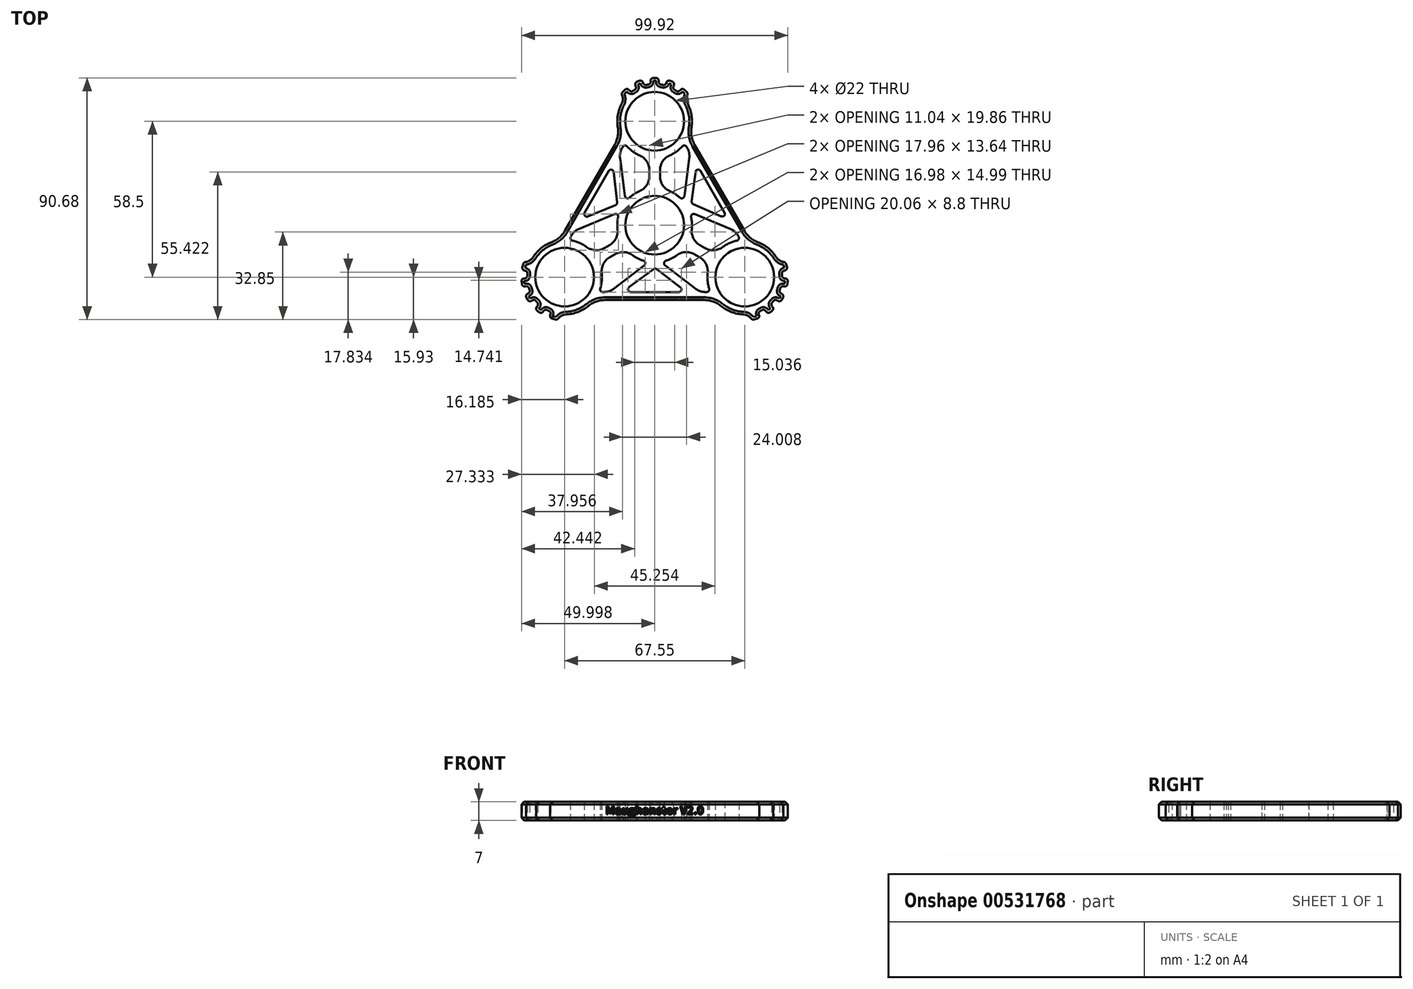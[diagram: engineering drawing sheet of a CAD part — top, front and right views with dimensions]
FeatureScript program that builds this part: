
annotation { "Feature Type Name" : "Feature", "Feature Type Description" : "" }
export const myFeature = defineFeature(function(context is Context, id is Id, definition is map)
    precondition{}
    {
        {
            var Q0;
            Q0=qCreatedBy(makeId("Top.planeOp"),FACE);
            var sketch = newSketch(context, id + "F0", { "sketchPlane" : qUnion([Q0])});
            skCircle(sketch, "E0", {"center": v(0, 0) * mm, "radius": 11 * mm});
            skArc(sketch, "E1.0", {"start": v(-2, 13.86) * mm, "mid": v(-6.9, 12.18) * mm, "end": v(-10.85, 8.84) * mm});
            skCircle(sketch, "E2", {"center": v(0, 39) * mm, "radius": 11 * mm});
            skArc(sketch, "E3.0", {"start": v(-10.9, 47.78) * mm, "mid": v(-13.85, 41.03) * mm, "end": v(-12.97, 33.72) * mm});
            skLineSegment(sketch, "E4", {"start": v(0, 11) * mm, "end": v(0, 28) * mm, "construction": true});
            skLineSegment(sketch, "E5.0", {"start": v(2, 13.86) * mm, "end": v(2, 25.14) * mm});
            skLineSegment(sketch, "E6.0", {"start": v(-2, 13.86) * mm, "end": v(-2, 25.14) * mm});
            skLineSegment(sketch, "E7", {"start": v(0, 53) * mm, "end": v(0, 55) * mm, "construction": true});
            skLineSegment(sketch, "E8.0", {"start": v(1.5, 52.92) * mm, "end": v(1.5, 55.25) * mm});
            skLineSegment(sketch, "E9.0", {"start": v(-1.5, 52.92) * mm, "end": v(-1.5, 55.25) * mm});
            skLineSegment(sketch, "E10", {"start": v(-1.5, 55.25) * mm, "end": v(1.5, 55.25) * mm});
            skLineSegment(sketch, "E11.1.0", {"start": v(4.83, 54.59) * mm, "end": v(7.6, 53.44) * mm});
            skLineSegment(sketch, "E11.1.1", {"start": v(3.94, 52.43) * mm, "end": v(4.83, 54.59) * mm});
            skLineSegment(sketch, "E11.1.2", {"start": v(6.71, 51.29) * mm, "end": v(7.6, 53.44) * mm});
            skLineSegment(sketch, "E11.2.0", {"start": v(10.43, 51.55) * mm, "end": v(12.55, 49.43) * mm});
            skLineSegment(sketch, "E11.2.1", {"start": v(8.78, 49.9) * mm, "end": v(10.43, 51.55) * mm});
            skLineSegment(sketch, "E11.2.2", {"start": v(10.9, 47.78) * mm, "end": v(12.55, 49.43) * mm});
            skLineSegment(sketch, "E11.anchor1", {"start": v(0, 39) * mm, "end": v(-1.5, 55.25) * mm, "construction": true});
            skLineSegment(sketch, "E11.anchor2", {"start": v(0, 39) * mm, "end": v(10.43, 51.55) * mm, "construction": true});
            skLineSegment(sketch, "E12.MirrorCS", {"start": v(-4.83, 54.59) * mm, "end": v(-7.6, 53.44) * mm});
            skLineSegment(sketch, "E13.MirrorCS", {"start": v(-3.94, 52.43) * mm, "end": v(-4.83, 54.59) * mm});
            skLineSegment(sketch, "E14.MirrorCS", {"start": v(-6.71, 51.29) * mm, "end": v(-7.6, 53.44) * mm});
            skLineSegment(sketch, "E15.MirrorCS", {"start": v(-8.78, 49.9) * mm, "end": v(-10.43, 51.55) * mm});
            skLineSegment(sketch, "E16.MirrorCS", {"start": v(-10.43, 51.55) * mm, "end": v(-12.55, 49.43) * mm});
            skLineSegment(sketch, "E17.MirrorCS", {"start": v(-10.9, 47.78) * mm, "end": v(-12.55, 49.43) * mm});
            skArc(sketch, "E18.trimOffspring", {"start": v(-6.71, 51.29) * mm, "mid": v(-7.78, 50.64) * mm, "end": v(-8.78, 49.9) * mm});
            skArc(sketch, "E19.trimOffspring", {"start": v(-1.29, 52.94) * mm, "mid": v(-2.63, 52.75) * mm, "end": v(-3.94, 52.43) * mm});
            skArc(sketch, "E20.trimOffspring", {"start": v(3.94, 52.43) * mm, "mid": v(2.73, 52.73) * mm, "end": v(1.5, 52.92) * mm});
            skArc(sketch, "E21.trimOffspring", {"start": v(8.95, 49.77) * mm, "mid": v(7.87, 50.58) * mm, "end": v(6.71, 51.29) * mm});
            skArc(sketch, "E22.trimOffspring", {"start": v(2, 25.14) * mm, "mid": v(7.18, 26.98) * mm, "end": v(11.26, 30.68) * mm});
            skLineSegment(sketch, "E23.1.0", {"start": v(-33.77, -19.5) * mm, "end": v(-47.1, -28.92) * mm, "construction": true});
            skPoint(sketch, "E23.1.1", {"position": v(-33.77, -19.5) * mm});
            skCircle(sketch, "E23.1.2", {"center": v(-33.77, -19.5) * mm, "radius": 11 * mm});
            skLineSegment(sketch, "E23.1.3", {"start": v(-9.53, -5.5) * mm, "end": v(-24.25, -14) * mm, "construction": true});
            skArc(sketch, "E23.1.4", {"start": v(-35.93, -33.33) * mm, "mid": v(-28.6, -32.51) * mm, "end": v(-22.72, -28.09) * mm});
            skLineSegment(sketch, "E23.1.5", {"start": v(-13, -5.2) * mm, "end": v(-22.77, -10.84) * mm});
            skLineSegment(sketch, "E23.1.6", {"start": v(-11, -8.66) * mm, "end": v(-20.77, -14.3) * mm});
            skLineSegment(sketch, "E23.1.7", {"start": v(-33.77, -19.5) * mm, "end": v(-49.86, -16.74) * mm, "construction": true});
            skArc(sketch, "E23.1.8", {"start": v(-22.77, -10.84) * mm, "mid": v(-26.96, -7.27) * mm, "end": v(-32.2, -5.59) * mm});
            skLineSegment(sketch, "E23.1.9", {"start": v(-41.06, -31.46) * mm, "end": v(-42.48, -33.3) * mm});
            skLineSegment(sketch, "E23.1.10", {"start": v(-35.93, -33.33) * mm, "end": v(-36.53, -35.58) * mm});
            skLineSegment(sketch, "E23.1.11", {"start": v(-49.86, -16.74) * mm, "end": v(-49.08, -13.85) * mm});
            skLineSegment(sketch, "E23.1.12", {"start": v(-47.77, -19.83) * mm, "end": v(-50.08, -20.13) * mm});
            skArc(sketch, "E23.1.13", {"start": v(-47.57, -17.13) * mm, "mid": v(-47.74, -18.48) * mm, "end": v(-47.77, -19.83) * mm});
            skLineSegment(sketch, "E23.1.14", {"start": v(-44.86, -31.48) * mm, "end": v(-42.48, -33.3) * mm});
            skLineSegment(sketch, "E23.1.15", {"start": v(-45.9, -26.5) * mm, "end": v(-47.63, -27.5) * mm, "construction": true});
            skLineSegment(sketch, "E23.1.16", {"start": v(-46.58, -25.16) * mm, "end": v(-48.6, -26.33) * mm});
            skLineSegment(sketch, "E23.1.17", {"start": v(-47.1, -28.92) * mm, "end": v(-48.6, -26.33) * mm});
            skLineSegment(sketch, "E23.1.18", {"start": v(-45.08, -27.76) * mm, "end": v(-47.1, -28.92) * mm});
            skLineSegment(sketch, "E23.1.19", {"start": v(-49.7, -23.1) * mm, "end": v(-50.08, -20.13) * mm});
            skLineSegment(sketch, "E23.1.20", {"start": v(-47.38, -22.8) * mm, "end": v(-49.7, -23.1) * mm});
            skArc(sketch, "E23.1.21", {"start": v(-47.38, -22.8) * mm, "mid": v(-47.03, -24) * mm, "end": v(-46.58, -25.16) * mm});
            skArc(sketch, "E23.1.22", {"start": v(-41.06, -31.46) * mm, "mid": v(-39.97, -32.06) * mm, "end": v(-38.83, -32.56) * mm});
            skLineSegment(sketch, "E23.1.23", {"start": v(-39.43, -34.8) * mm, "end": v(-36.53, -35.58) * mm});
            skLineSegment(sketch, "E23.1.24", {"start": v(-43.44, -29.63) * mm, "end": v(-44.86, -31.48) * mm});
            skLineSegment(sketch, "E23.1.25", {"start": v(-46.83, -14.45) * mm, "end": v(-49.08, -13.85) * mm});
            skArc(sketch, "E23.1.26", {"start": v(-45.2, -27.58) * mm, "mid": v(-44.37, -28.65) * mm, "end": v(-43.44, -29.63) * mm});
            skLineSegment(sketch, "E23.1.27", {"start": v(-38.83, -32.56) * mm, "end": v(-39.43, -34.8) * mm});
            skLineSegment(sketch, "E23.1.28", {"start": v(-47.6, -17.35) * mm, "end": v(-49.86, -16.74) * mm});
            skLineSegment(sketch, "E23.2.0", {"start": v(33.77, -19.5) * mm, "end": v(48.6, -26.33) * mm, "construction": true});
            skPoint(sketch, "E23.2.1", {"position": v(33.77, -19.5) * mm});
            skCircle(sketch, "E23.2.2", {"center": v(33.77, -19.5) * mm, "radius": 11 * mm});
            skLineSegment(sketch, "E23.2.3", {"start": v(9.53, -5.5) * mm, "end": v(24.25, -14) * mm, "construction": true});
            skArc(sketch, "E23.2.4", {"start": v(46.83, -14.45) * mm, "mid": v(42.46, -8.52) * mm, "end": v(35.69, -5.63) * mm});
            skLineSegment(sketch, "E23.2.5", {"start": v(11, -8.66) * mm, "end": v(20.77, -14.3) * mm});
            skLineSegment(sketch, "E23.2.6", {"start": v(13, -5.2) * mm, "end": v(22.77, -10.84) * mm});
            skLineSegment(sketch, "E23.2.7", {"start": v(33.77, -19.5) * mm, "end": v(39.43, -34.8) * mm, "construction": true});
            skArc(sketch, "E23.2.8", {"start": v(20.77, -14.3) * mm, "mid": v(19.78, -19.71) * mm, "end": v(20.94, -25.09) * mm});
            skLineSegment(sketch, "E23.2.9", {"start": v(47.77, -19.83) * mm, "end": v(50.08, -20.13) * mm});
            skLineSegment(sketch, "E23.2.10", {"start": v(46.83, -14.45) * mm, "end": v(49.08, -13.85) * mm});
            skLineSegment(sketch, "E23.2.11", {"start": v(39.43, -34.8) * mm, "end": v(36.53, -35.58) * mm});
            skLineSegment(sketch, "E23.2.12", {"start": v(41.06, -31.46) * mm, "end": v(42.48, -33.3) * mm});
            skArc(sketch, "E23.2.13", {"start": v(38.63, -32.63) * mm, "mid": v(39.87, -32.1) * mm, "end": v(41.06, -31.46) * mm});
            skLineSegment(sketch, "E23.2.14", {"start": v(49.7, -23.1) * mm, "end": v(50.08, -20.13) * mm});
            skLineSegment(sketch, "E23.2.15", {"start": v(45.9, -26.5) * mm, "end": v(47.63, -27.5) * mm, "construction": true});
            skLineSegment(sketch, "E23.2.16", {"start": v(45.08, -27.76) * mm, "end": v(47.1, -28.92) * mm});
            skLineSegment(sketch, "E23.2.17", {"start": v(48.6, -26.33) * mm, "end": v(47.1, -28.92) * mm});
            skLineSegment(sketch, "E23.2.18", {"start": v(46.58, -25.16) * mm, "end": v(48.6, -26.33) * mm});
            skLineSegment(sketch, "E23.2.19", {"start": v(44.86, -31.48) * mm, "end": v(42.48, -33.3) * mm});
            skLineSegment(sketch, "E23.2.20", {"start": v(43.44, -29.63) * mm, "end": v(44.86, -31.48) * mm});
            skArc(sketch, "E23.2.21", {"start": v(43.44, -29.63) * mm, "mid": v(44.3, -28.73) * mm, "end": v(45.08, -27.76) * mm});
            skArc(sketch, "E23.2.22", {"start": v(47.77, -19.83) * mm, "mid": v(47.75, -18.58) * mm, "end": v(47.6, -17.35) * mm});
            skLineSegment(sketch, "E23.2.23", {"start": v(49.86, -16.74) * mm, "end": v(49.08, -13.85) * mm});
            skLineSegment(sketch, "E23.2.24", {"start": v(47.38, -22.8) * mm, "end": v(49.7, -23.1) * mm});
            skLineSegment(sketch, "E23.2.25", {"start": v(35.93, -33.33) * mm, "end": v(36.53, -35.58) * mm});
            skArc(sketch, "E23.2.26", {"start": v(46.5, -25.36) * mm, "mid": v(47, -24.1) * mm, "end": v(47.38, -22.8) * mm});
            skLineSegment(sketch, "E23.2.27", {"start": v(47.6, -17.35) * mm, "end": v(49.86, -16.74) * mm});
            skLineSegment(sketch, "E23.2.28", {"start": v(38.83, -32.56) * mm, "end": v(39.43, -34.8) * mm});
            skArc(sketch, "E24.trimOffspring", {"start": v(13, -5.2) * mm, "mid": v(14, -0.12) * mm, "end": v(13.09, 4.98) * mm});
            skArc(sketch, "E25.trimOffspring", {"start": v(-11, -8.66) * mm, "mid": v(-7.1, -12.06) * mm, "end": v(-2.23, -13.82) * mm});
            skLineSegment(sketch, "E26", {"start": v(-12.97, 33.72) * mm, "end": v(-35.69, -5.63) * mm});
            skLineSegment(sketch, "E27.0", {"start": v(-11.26, 30.68) * mm, "end": v(-13.25, 27.23) * mm});
            skArc(sketch, "E28.trimOffspring", {"start": v(-11.26, 30.68) * mm, "mid": v(-7.18, 26.98) * mm, "end": v(-2, 25.14) * mm});
            skArc(sketch, "E29.trimOffspring", {"start": v(-35.69, -5.63) * mm, "mid": v(-42.46, -8.52) * mm, "end": v(-46.83, -14.45) * mm});
            skLineSegment(sketch, "E30", {"start": v(-12.12, 7) * mm, "end": v(-28.97, 0) * mm, "construction": true});
            skLineSegment(sketch, "E31", {"start": v(-12.12, 7) * mm, "end": v(-21.73, 12.54) * mm, "construction": true});
            skLineSegment(sketch, "E32.0", {"start": v(-13.98, 7.85) * mm, "end": v(-27.74, 2.14) * mm});
            skLineSegment(sketch, "E33.0", {"start": v(-13.09, 4.98) * mm, "end": v(-30.2, -2.14) * mm});
            skLineSegment(sketch, "E34.trimOffspring", {"start": v(-30.2, -2.14) * mm, "end": v(-32.2, -5.59) * mm});
            skArc(sketch, "E35.trimOffspring", {"start": v(-13.09, 4.98) * mm, "mid": v(-14, -0.12) * mm, "end": v(-13, -5.2) * mm});
            skLineSegment(sketch, "E36.MirrorCS", {"start": v(-10.85, 8.84) * mm, "end": v(-13.25, 27.23) * mm});
            skLineSegment(sketch, "E37.trimOffspring", {"start": v(-15.72, 22.95) * mm, "end": v(-27.74, 2.14) * mm});
            skPoint(sketch, "E38.orphan", {"position": v(-10.45, 9.32) * mm});
            skLineSegment(sketch, "E39.trimOffspring", {"start": v(-13.98, 7.85) * mm, "end": v(-15.72, 22.95) * mm});
            skPoint(sketch, "E40.MirrorCS.start.orphan", {"position": v(-13.3, 4.38) * mm});
            skLineSegment(sketch, "E41.1.0", {"start": v(-22.72, -28.09) * mm, "end": v(22.72, -28.09) * mm});
            skLineSegment(sketch, "E41.1.1", {"start": v(0.2, -16.04) * mm, "end": v(-12.02, -25.09) * mm});
            skLineSegment(sketch, "E41.1.2", {"start": v(0, -14) * mm, "end": v(0, -25.09) * mm, "construction": true});
            skLineSegment(sketch, "E41.1.3", {"start": v(-12.02, -25.09) * mm, "end": v(12.02, -25.09) * mm});
            skLineSegment(sketch, "E41.1.4", {"start": v(-2.23, -13.82) * mm, "end": v(-16.95, -25.09) * mm});
            skLineSegment(sketch, "E41.1.5", {"start": v(16.95, -25.09) * mm, "end": v(20.94, -25.09) * mm});
            skLineSegment(sketch, "E41.1.6", {"start": v(2.23, -13.82) * mm, "end": v(16.95, -25.09) * mm});
            skLineSegment(sketch, "E41.1.7", {"start": v(0.2, -16.04) * mm, "end": v(12.02, -25.09) * mm});
            skLineSegment(sketch, "E41.1.8", {"start": v(0, -14) * mm, "end": v(14.49, -25.09) * mm, "construction": true});
            skLineSegment(sketch, "E41.1.9", {"start": v(-20.94, -25.09) * mm, "end": v(-16.95, -25.09) * mm});
            skLineSegment(sketch, "E41.2.0", {"start": v(35.69, -5.63) * mm, "end": v(12.97, 33.72) * mm});
            skLineSegment(sketch, "E41.2.1", {"start": v(13.8, 8.18) * mm, "end": v(27.74, 2.14) * mm});
            skLineSegment(sketch, "E41.2.2", {"start": v(12.12, 7) * mm, "end": v(21.73, 12.54) * mm, "construction": true});
            skLineSegment(sketch, "E41.2.3", {"start": v(27.74, 2.14) * mm, "end": v(15.72, 22.95) * mm});
            skLineSegment(sketch, "E41.2.4", {"start": v(13.09, 4.98) * mm, "end": v(30.2, -2.14) * mm});
            skLineSegment(sketch, "E41.2.5", {"start": v(13.25, 27.23) * mm, "end": v(11.26, 30.68) * mm});
            skLineSegment(sketch, "E41.2.6", {"start": v(10.85, 8.84) * mm, "end": v(13.25, 27.23) * mm});
            skLineSegment(sketch, "E41.2.7", {"start": v(13.8, 8.18) * mm, "end": v(15.72, 22.95) * mm});
            skLineSegment(sketch, "E41.2.8", {"start": v(12.12, 7) * mm, "end": v(14.49, 25.09) * mm, "construction": true});
            skLineSegment(sketch, "E41.2.9", {"start": v(32.2, -5.59) * mm, "end": v(30.2, -2.14) * mm});
            skArc(sketch, "E42.trimOffspring", {"start": v(12.97, 33.72) * mm, "mid": v(13.85, 41.03) * mm, "end": v(10.9, 47.78) * mm});
            skArc(sketch, "E43.trimOffspring", {"start": v(32.2, -5.59) * mm, "mid": v(26.96, -7.27) * mm, "end": v(22.77, -10.84) * mm});
            skArc(sketch, "E44.trimOffspring", {"start": v(10.85, 8.84) * mm, "mid": v(6.9, 12.18) * mm, "end": v(2, 13.86) * mm});
            skArc(sketch, "E45.trimOffspring", {"start": v(2.23, -13.82) * mm, "mid": v(7.1, -12.06) * mm, "end": v(11, -8.66) * mm});
            skArc(sketch, "E46.trimOffspring", {"start": v(22.72, -28.09) * mm, "mid": v(28.6, -32.51) * mm, "end": v(35.93, -33.33) * mm});
            skArc(sketch, "E47.trimOffspring", {"start": v(-20.94, -25.09) * mm, "mid": v(-19.78, -19.71) * mm, "end": v(-20.77, -14.3) * mm});
            skSolve(sketch);
        }
        {
            var Q0;
            Q0=qSketchRegion(id+"F0",true);
            extrude(context, id + "F1", {"entities" : qUnion([Q0]), "depth" : 7 * mm});
        }
        {
            var Q0;
            Q0=makeQuery(id+"F1.opExtrude","SWEPT_EDGE",EDGE,{"disambiguationData":[OSD([sQuery(id+"F0.wireOp",EDGE,"E1.0"),sQuery(id+"F0.wireOp",EDGE,"E6.0")])]});
            var Q1;
            Q1=makeQuery(id+"F1.opExtrude","SWEPT_EDGE",EDGE,{"disambiguationData":[OSD([sQuery(id+"F0.wireOp",EDGE,"E5.0"),sQuery(id+"F0.wireOp",EDGE,"E44.trimOffspring")])]});
            var Q2;
            Q2=makeQuery(id+"F1.opExtrude","SWEPT_EDGE",EDGE,{"disambiguationData":[OSD([sQuery(id+"F0.wireOp",EDGE,"E5.0"),sQuery(id+"F0.wireOp",EDGE,"E22.trimOffspring")])]});
            var Q3;
            Q3=makeQuery(id+"F1.opExtrude","SWEPT_EDGE",EDGE,{"disambiguationData":[OSD([sQuery(id+"F0.wireOp",EDGE,"E6.0"),sQuery(id+"F0.wireOp",EDGE,"E28.trimOffspring")])]});
            var Q4;
            Q4=makeQuery(id+"F1.opExtrude","SWEPT_EDGE",EDGE,{"disambiguationData":[OSD([sQuery(id+"F0.wireOp",EDGE,"E23.1.5"),sQuery(id+"F0.wireOp",EDGE,"E35.trimOffspring")])]});
            var Q5;
            Q5=makeQuery(id+"F1.opExtrude","SWEPT_EDGE",EDGE,{"disambiguationData":[OSD([sQuery(id+"F0.wireOp",EDGE,"E23.2.5"),sQuery(id+"F0.wireOp",EDGE,"E23.2.8")])]});
            var Q6;
            Q6=makeQuery(id+"F1.opExtrude","SWEPT_EDGE",EDGE,{"disambiguationData":[OSD([sQuery(id+"F0.wireOp",EDGE,"E23.1.6"),sQuery(id+"F0.wireOp",EDGE,"E47.trimOffspring")])]});
            var Q7;
            Q7=makeQuery(id+"F1.opExtrude","SWEPT_EDGE",EDGE,{"disambiguationData":[OSD([sQuery(id+"F0.wireOp",EDGE,"E23.1.6"),sQuery(id+"F0.wireOp",EDGE,"E25.trimOffspring")])]});
            var Q8;
            Q8=makeQuery(id+"F1.opExtrude","SWEPT_EDGE",EDGE,{"disambiguationData":[OSD([sQuery(id+"F0.wireOp",EDGE,"E23.1.5"),sQuery(id+"F0.wireOp",EDGE,"E23.1.8")])]});
            var Q9;
            Q9=makeQuery(id+"F1.opExtrude","SWEPT_EDGE",EDGE,{"disambiguationData":[OSD([sQuery(id+"F0.wireOp",EDGE,"E23.2.6"),sQuery(id+"F0.wireOp",EDGE,"E43.trimOffspring")])]});
            var Q10;
            Q10=makeQuery(id+"F1.opExtrude","SWEPT_EDGE",EDGE,{"disambiguationData":[OSD([sQuery(id+"F0.wireOp",EDGE,"E23.2.5"),sQuery(id+"F0.wireOp",EDGE,"E45.trimOffspring")])]});
            var Q11;
            Q11=makeQuery(id+"F1.opExtrude","SWEPT_EDGE",EDGE,{"disambiguationData":[OSD([sQuery(id+"F0.wireOp",EDGE,"E23.2.6"),sQuery(id+"F0.wireOp",EDGE,"E24.trimOffspring")])]});
            var Q12;
            Q12=makeQuery(id+"F1.opExtrude","SWEPT_EDGE",EDGE,{"disambiguationData":[OSD([sQuery(id+"F0.wireOp",EDGE,"E33.0"),sQuery(id+"F0.wireOp",EDGE,"E34.trimOffspring")])]});
            var Q13;
            Q13=makeQuery(id+"F1.opExtrude","SWEPT_EDGE",EDGE,{"disambiguationData":[OSD([sQuery(id+"F0.wireOp",EDGE,"E41.1.4"),sQuery(id+"F0.wireOp",EDGE,"E41.1.9")])]});
            var Q14;
            Q14=makeQuery(id+"F1.opExtrude","SWEPT_EDGE",EDGE,{"disambiguationData":[OSD([sQuery(id+"F0.wireOp",EDGE,"E41.1.5"),sQuery(id+"F0.wireOp",EDGE,"E41.1.6")])]});
            var Q15;
            Q15=makeQuery(id+"F1.opExtrude","SWEPT_EDGE",EDGE,{"disambiguationData":[OSD([sQuery(id+"F0.wireOp",EDGE,"E41.2.5"),sQuery(id+"F0.wireOp",EDGE,"E41.2.6")])]});
            var Q16;
            Q16=makeQuery(id+"F1.opExtrude","SWEPT_EDGE",EDGE,{"disambiguationData":[OSD([sQuery(id+"F0.wireOp",EDGE,"E41.2.4"),sQuery(id+"F0.wireOp",EDGE,"E41.2.9")])]});
            var Q17;
            Q17=makeQuery(id+"F1.opExtrude","SWEPT_EDGE",EDGE,{"disambiguationData":[OSD([sQuery(id+"F0.wireOp",EDGE,"E27.0"),sQuery(id+"F0.wireOp",EDGE,"E36.MirrorCS")])]});
            fillet(context, id + "F2", {"entities" : qUnion([Q0, Q1, Q2, Q3, Q4, Q5, Q6, Q7, Q8, Q9, Q10, Q11, Q12, Q13, Q14, Q15, Q16, Q17]), "radius" : 6 * mm, "tangentPropagation" : true, "allowEdgeOverflow" : false});
        }
        {
            var Q0;
            Q0=makeQuery(id+"F1.opExtrude","SWEPT_EDGE",EDGE,{"disambiguationData":[OSD([sQuery(id+"F0.wireOp",EDGE,"E1.0"),sQuery(id+"F0.wireOp",EDGE,"E36.MirrorCS")])]});
            var Q1;
            Q1=makeQuery(id+"F1.opExtrude","SWEPT_EDGE",EDGE,{"disambiguationData":[OSD([sQuery(id+"F0.wireOp",EDGE,"E33.0"),sQuery(id+"F0.wireOp",EDGE,"E35.trimOffspring")])]});
            var Q2;
            Q2=makeQuery(id+"F1.opExtrude","SWEPT_EDGE",EDGE,{"disambiguationData":[OSD([sQuery(id+"F0.wireOp",EDGE,"E25.trimOffspring"),sQuery(id+"F0.wireOp",EDGE,"E41.1.4")])]});
            var Q3;
            Q3=makeQuery(id+"F1.opExtrude","SWEPT_EDGE",EDGE,{"disambiguationData":[OSD([sQuery(id+"F0.wireOp",EDGE,"E41.1.6"),sQuery(id+"F0.wireOp",EDGE,"E45.trimOffspring")])]});
            var Q4;
            Q4=makeQuery(id+"F1.opExtrude","SWEPT_EDGE",EDGE,{"disambiguationData":[OSD([sQuery(id+"F0.wireOp",EDGE,"E24.trimOffspring"),sQuery(id+"F0.wireOp",EDGE,"E41.2.4")])]});
            var Q5;
            Q5=makeQuery(id+"F1.opExtrude","SWEPT_EDGE",EDGE,{"disambiguationData":[OSD([sQuery(id+"F0.wireOp",EDGE,"E41.2.6"),sQuery(id+"F0.wireOp",EDGE,"E44.trimOffspring")])]});
            var Q6;
            Q6=makeQuery(id+"F1.opExtrude","SWEPT_EDGE",EDGE,{"disambiguationData":[OSD([sQuery(id+"F0.wireOp",EDGE,"E41.2.9"),sQuery(id+"F0.wireOp",EDGE,"E43.trimOffspring")])]});
            var Q7;
            Q7=makeQuery(id+"F1.opExtrude","SWEPT_EDGE",EDGE,{"disambiguationData":[OSD([sQuery(id+"F0.wireOp",EDGE,"E23.2.8"),sQuery(id+"F0.wireOp",EDGE,"E41.1.5")])]});
            var Q8;
            Q8=makeQuery(id+"F1.opExtrude","SWEPT_EDGE",EDGE,{"disambiguationData":[OSD([sQuery(id+"F0.wireOp",EDGE,"E41.1.9"),sQuery(id+"F0.wireOp",EDGE,"E47.trimOffspring")])]});
            var Q9;
            Q9=makeQuery(id+"F1.opExtrude","SWEPT_EDGE",EDGE,{"disambiguationData":[OSD([sQuery(id+"F0.wireOp",EDGE,"E23.1.8"),sQuery(id+"F0.wireOp",EDGE,"E34.trimOffspring")])]});
            var Q10;
            Q10=makeQuery(id+"F1.opExtrude","SWEPT_EDGE",EDGE,{"disambiguationData":[OSD([sQuery(id+"F0.wireOp",EDGE,"E22.trimOffspring"),sQuery(id+"F0.wireOp",EDGE,"E41.2.5")])]});
            var Q11;
            Q11=makeQuery(id+"F1.opExtrude","SWEPT_EDGE",EDGE,{"disambiguationData":[OSD([sQuery(id+"F0.wireOp",EDGE,"E27.0"),sQuery(id+"F0.wireOp",EDGE,"E28.trimOffspring")])]});
            var Q12;
            Q12=makeQuery(id+"F1.opExtrude","SWEPT_EDGE",EDGE,{"disambiguationData":[OSD([sQuery(id+"F0.wireOp",EDGE,"E37.trimOffspring"),sQuery(id+"F0.wireOp",EDGE,"E39.trimOffspring")])]});
            var Q13;
            Q13=makeQuery(id+"F1.opExtrude","SWEPT_EDGE",EDGE,{"disambiguationData":[OSD([sQuery(id+"F0.wireOp",EDGE,"E32.0"),sQuery(id+"F0.wireOp",EDGE,"E37.trimOffspring")])]});
            var Q14;
            Q14=makeQuery(id+"F1.opExtrude","SWEPT_EDGE",EDGE,{"disambiguationData":[OSD([sQuery(id+"F0.wireOp",EDGE,"E41.2.1"),sQuery(id+"F0.wireOp",EDGE,"E41.2.3")])]});
            var Q15;
            Q15=makeQuery(id+"F1.opExtrude","SWEPT_EDGE",EDGE,{"disambiguationData":[OSD([sQuery(id+"F0.wireOp",EDGE,"E41.2.3"),sQuery(id+"F0.wireOp",EDGE,"E41.2.7")])]});
            var Q16;
            Q16=makeQuery(id+"F1.opExtrude","SWEPT_EDGE",EDGE,{"disambiguationData":[OSD([sQuery(id+"F0.wireOp",EDGE,"E41.1.3"),sQuery(id+"F0.wireOp",EDGE,"E41.1.7")])]});
            var Q17;
            Q17=makeQuery(id+"F1.opExtrude","SWEPT_EDGE",EDGE,{"disambiguationData":[OSD([sQuery(id+"F0.wireOp",EDGE,"E41.1.1"),sQuery(id+"F0.wireOp",EDGE,"E41.1.3")])]});
            var Q18;
            Q18=makeQuery(id+"F1.opExtrude","SWEPT_EDGE",EDGE,{"disambiguationData":[OSD([sQuery(id+"F0.wireOp",EDGE,"E32.0"),sQuery(id+"F0.wireOp",EDGE,"E39.trimOffspring")])]});
            var Q19;
            Q19=makeQuery(id+"F1.opExtrude","SWEPT_EDGE",EDGE,{"disambiguationData":[OSD([sQuery(id+"F0.wireOp",EDGE,"E41.1.1"),sQuery(id+"F0.wireOp",EDGE,"E41.1.7")])]});
            var Q20;
            Q20=makeQuery(id+"F1.opExtrude","SWEPT_EDGE",EDGE,{"disambiguationData":[OSD([sQuery(id+"F0.wireOp",EDGE,"E41.2.1"),sQuery(id+"F0.wireOp",EDGE,"E41.2.7")])]});
            fillet(context, id + "F3", {"entities" : qUnion([Q0, Q1, Q2, Q3, Q4, Q5, Q6, Q7, Q8, Q9, Q10, Q11, Q12, Q13, Q14, Q15, Q16, Q17, Q18, Q19, Q20]), "radius" : 1 * mm, "tangentPropagation" : true, "allowEdgeOverflow" : false});
        }
        {
            var Q0;
            Q0=makeQuery(id+"F1.opExtrude","SWEPT_EDGE",EDGE,{"disambiguationData":[OSD([sQuery(id+"F0.wireOp",EDGE,"E3.0"),sQuery(id+"F0.wireOp",EDGE,"E26")])]});
            var Q1;
            Q1=makeQuery(id+"F1.opExtrude","SWEPT_EDGE",EDGE,{"disambiguationData":[OSD([sQuery(id+"F0.wireOp",EDGE,"E41.2.0"),sQuery(id+"F0.wireOp",EDGE,"E42.trimOffspring")])]});
            var Q2;
            Q2=makeQuery(id+"F1.opExtrude","SWEPT_EDGE",EDGE,{"disambiguationData":[OSD([sQuery(id+"F0.wireOp",EDGE,"E26"),sQuery(id+"F0.wireOp",EDGE,"E29.trimOffspring")])]});
            var Q3;
            Q3=makeQuery(id+"F1.opExtrude","SWEPT_EDGE",EDGE,{"disambiguationData":[OSD([sQuery(id+"F0.wireOp",EDGE,"E23.1.4"),sQuery(id+"F0.wireOp",EDGE,"E41.1.0")])]});
            var Q4;
            Q4=makeQuery(id+"F1.opExtrude","SWEPT_EDGE",EDGE,{"disambiguationData":[OSD([sQuery(id+"F0.wireOp",EDGE,"E41.1.0"),sQuery(id+"F0.wireOp",EDGE,"E46.trimOffspring")])]});
            var Q5;
            Q5=makeQuery(id+"F1.opExtrude","SWEPT_EDGE",EDGE,{"disambiguationData":[OSD([sQuery(id+"F0.wireOp",EDGE,"E23.2.4"),sQuery(id+"F0.wireOp",EDGE,"E41.2.0")])]});
            fillet(context, id + "F4", {"entities" : qUnion([Q0, Q1, Q2, Q3, Q4, Q5]), "radius" : 10 * mm, "tangentPropagation" : true, "allowEdgeOverflow" : false});
        }
        {
            var Q0;
            Q0=makeQuery(id+"F1.opExtrude","SWEPT_EDGE",EDGE,{"disambiguationData":[OSD([sQuery(id+"F0.wireOp",EDGE,"E3.0"),sQuery(id+"F0.wireOp",EDGE,"E17.MirrorCS")])]});
            var Q1;
            Q1=makeQuery(id+"F1.opExtrude","SWEPT_EDGE",EDGE,{"disambiguationData":[OSD([sQuery(id+"F0.wireOp",EDGE,"E11.2.2"),sQuery(id+"F0.wireOp",EDGE,"E42.trimOffspring")])]});
            var Q2;
            Q2=makeQuery(id+"F1.opExtrude","SWEPT_EDGE",EDGE,{"disambiguationData":[OSD([sQuery(id+"F0.wireOp",EDGE,"E23.1.25"),sQuery(id+"F0.wireOp",EDGE,"E29.trimOffspring")])]});
            var Q3;
            Q3=makeQuery(id+"F1.opExtrude","SWEPT_EDGE",EDGE,{"disambiguationData":[OSD([sQuery(id+"F0.wireOp",EDGE,"E23.1.4"),sQuery(id+"F0.wireOp",EDGE,"E23.1.10")])]});
            var Q4;
            Q4=makeQuery(id+"F1.opExtrude","SWEPT_EDGE",EDGE,{"disambiguationData":[OSD([sQuery(id+"F0.wireOp",EDGE,"E23.2.25"),sQuery(id+"F0.wireOp",EDGE,"E46.trimOffspring")])]});
            var Q5;
            Q5=makeQuery(id+"F1.opExtrude","SWEPT_EDGE",EDGE,{"disambiguationData":[OSD([sQuery(id+"F0.wireOp",EDGE,"E23.2.4"),sQuery(id+"F0.wireOp",EDGE,"E23.2.10")])]});
            fillet(context, id + "F5", {"entities" : qUnion([Q0, Q1, Q2, Q3, Q4, Q5]), "radius" : 4 * mm, "tangentPropagation" : true, "allowEdgeOverflow" : false});
        }
        {
            var Q0;
            Q0=makeQuery(id+"F1.opExtrude","SWEPT_EDGE",EDGE,{"disambiguationData":[OSD([sQuery(id+"F0.wireOp",EDGE,"E15.MirrorCS"),sQuery(id+"F0.wireOp",EDGE,"E18.trimOffspring")])]});
            var Q1;
            Q1=makeQuery(id+"F1.opExtrude","SWEPT_EDGE",EDGE,{"disambiguationData":[OSD([sQuery(id+"F0.wireOp",EDGE,"E14.MirrorCS"),sQuery(id+"F0.wireOp",EDGE,"E18.trimOffspring")])]});
            var Q2;
            Q2=makeQuery(id+"F1.opExtrude","SWEPT_EDGE",EDGE,{"disambiguationData":[OSD([sQuery(id+"F0.wireOp",EDGE,"E13.MirrorCS"),sQuery(id+"F0.wireOp",EDGE,"E19.trimOffspring")])]});
            var Q3;
            Q3=makeQuery(id+"F1.opExtrude","SWEPT_EDGE",EDGE,{"disambiguationData":[OSD([sQuery(id+"F0.wireOp",EDGE,"E9.0"),sQuery(id+"F0.wireOp",EDGE,"E19.trimOffspring")])]});
            var Q4;
            Q4=makeQuery(id+"F1.opExtrude","SWEPT_EDGE",EDGE,{"disambiguationData":[OSD([sQuery(id+"F0.wireOp",EDGE,"E8.0"),sQuery(id+"F0.wireOp",EDGE,"E20.trimOffspring")])]});
            var Q5;
            Q5=makeQuery(id+"F1.opExtrude","SWEPT_EDGE",EDGE,{"disambiguationData":[OSD([sQuery(id+"F0.wireOp",EDGE,"E11.1.2"),sQuery(id+"F0.wireOp",EDGE,"E21.trimOffspring")])]});
            var Q6;
            Q6=makeQuery(id+"F1.opExtrude","SWEPT_EDGE",EDGE,{"disambiguationData":[OSD([sQuery(id+"F0.wireOp",EDGE,"E11.1.1"),sQuery(id+"F0.wireOp",EDGE,"E20.trimOffspring")])]});
            var Q7;
            Q7=makeQuery(id+"F1.opExtrude","SWEPT_EDGE",EDGE,{"disambiguationData":[OSD([sQuery(id+"F0.wireOp",EDGE,"E11.2.1"),sQuery(id+"F0.wireOp",EDGE,"E21.trimOffspring")])]});
            var Q8;
            Q8=makeQuery(id+"F1.opExtrude","SWEPT_EDGE",EDGE,{"disambiguationData":[OSD([sQuery(id+"F0.wireOp",EDGE,"E23.1.13"),sQuery(id+"F0.wireOp",EDGE,"E23.1.28")])]});
            var Q9;
            Q9=makeQuery(id+"F1.opExtrude","SWEPT_EDGE",EDGE,{"disambiguationData":[OSD([sQuery(id+"F0.wireOp",EDGE,"E23.1.20"),sQuery(id+"F0.wireOp",EDGE,"E23.1.21")])]});
            var Q10;
            Q10=makeQuery(id+"F1.opExtrude","SWEPT_EDGE",EDGE,{"disambiguationData":[OSD([sQuery(id+"F0.wireOp",EDGE,"E23.1.9"),sQuery(id+"F0.wireOp",EDGE,"E23.1.22")])]});
            var Q11;
            Q11=makeQuery(id+"F1.opExtrude","SWEPT_EDGE",EDGE,{"disambiguationData":[OSD([sQuery(id+"F0.wireOp",EDGE,"E23.1.18"),sQuery(id+"F0.wireOp",EDGE,"E23.1.26")])]});
            var Q12;
            Q12=makeQuery(id+"F1.opExtrude","SWEPT_EDGE",EDGE,{"disambiguationData":[OSD([sQuery(id+"F0.wireOp",EDGE,"E23.1.12"),sQuery(id+"F0.wireOp",EDGE,"E23.1.13")])]});
            var Q13;
            Q13=makeQuery(id+"F1.opExtrude","SWEPT_EDGE",EDGE,{"disambiguationData":[OSD([sQuery(id+"F0.wireOp",EDGE,"E23.1.16"),sQuery(id+"F0.wireOp",EDGE,"E23.1.21")])]});
            var Q14;
            Q14=makeQuery(id+"F1.opExtrude","SWEPT_EDGE",EDGE,{"disambiguationData":[OSD([sQuery(id+"F0.wireOp",EDGE,"E23.1.24"),sQuery(id+"F0.wireOp",EDGE,"E23.1.26")])]});
            var Q15;
            Q15=makeQuery(id+"F1.opExtrude","SWEPT_EDGE",EDGE,{"disambiguationData":[OSD([sQuery(id+"F0.wireOp",EDGE,"E23.1.22"),sQuery(id+"F0.wireOp",EDGE,"E23.1.27")])]});
            var Q16;
            Q16=makeQuery(id+"F1.opExtrude","SWEPT_EDGE",EDGE,{"disambiguationData":[OSD([sQuery(id+"F0.wireOp",EDGE,"E23.2.22"),sQuery(id+"F0.wireOp",EDGE,"E23.2.27")])]});
            var Q17;
            Q17=makeQuery(id+"F1.opExtrude","SWEPT_EDGE",EDGE,{"disambiguationData":[OSD([sQuery(id+"F0.wireOp",EDGE,"E23.2.24"),sQuery(id+"F0.wireOp",EDGE,"E23.2.26")])]});
            var Q18;
            Q18=makeQuery(id+"F1.opExtrude","SWEPT_EDGE",EDGE,{"disambiguationData":[OSD([sQuery(id+"F0.wireOp",EDGE,"E23.2.16"),sQuery(id+"F0.wireOp",EDGE,"E23.2.21")])]});
            var Q19;
            Q19=makeQuery(id+"F1.opExtrude","SWEPT_EDGE",EDGE,{"disambiguationData":[OSD([sQuery(id+"F0.wireOp",EDGE,"E23.2.12"),sQuery(id+"F0.wireOp",EDGE,"E23.2.13")])]});
            var Q20;
            Q20=makeQuery(id+"F1.opExtrude","SWEPT_EDGE",EDGE,{"disambiguationData":[OSD([sQuery(id+"F0.wireOp",EDGE,"E23.2.13"),sQuery(id+"F0.wireOp",EDGE,"E23.2.28")])]});
            var Q21;
            Q21=makeQuery(id+"F1.opExtrude","SWEPT_EDGE",EDGE,{"disambiguationData":[OSD([sQuery(id+"F0.wireOp",EDGE,"E23.2.20"),sQuery(id+"F0.wireOp",EDGE,"E23.2.21")])]});
            var Q22;
            Q22=makeQuery(id+"F1.opExtrude","SWEPT_EDGE",EDGE,{"disambiguationData":[OSD([sQuery(id+"F0.wireOp",EDGE,"E23.2.18"),sQuery(id+"F0.wireOp",EDGE,"E23.2.26")])]});
            var Q23;
            Q23=makeQuery(id+"F1.opExtrude","SWEPT_EDGE",EDGE,{"disambiguationData":[OSD([sQuery(id+"F0.wireOp",EDGE,"E23.2.9"),sQuery(id+"F0.wireOp",EDGE,"E23.2.22")])]});
            fillet(context, id + "F6", {"entities" : qUnion([Q0, Q1, Q2, Q3, Q4, Q5, Q6, Q7, Q8, Q9, Q10, Q11, Q12, Q13, Q14, Q15, Q16, Q17, Q18, Q19, Q20, Q21, Q22, Q23]), "radius" : 1 * mm, "tangentPropagation" : true, "allowEdgeOverflow" : false});
        }
        {
            var Q0;
            Q0=makeQuery(id+"F1.opExtrude","SWEPT_EDGE",EDGE,{"disambiguationData":[OSD([sQuery(id+"F0.wireOp",EDGE,"E12.MirrorCS"),sQuery(id+"F0.wireOp",EDGE,"E14.MirrorCS")])]});
            var Q1;
            Q1=makeQuery(id+"F1.opExtrude","SWEPT_EDGE",EDGE,{"disambiguationData":[OSD([sQuery(id+"F0.wireOp",EDGE,"E12.MirrorCS"),sQuery(id+"F0.wireOp",EDGE,"E13.MirrorCS")])]});
            var Q2;
            Q2=makeQuery(id+"F5.opFillet","BLEND_EDGE",EDGE,{"blendedFrom":[makeQuery(id+"F1.opExtrude","SWEPT_EDGE",EDGE,{"disambiguationData":[OSD([sQuery(id+"F0.wireOp",EDGE,"E3.0"),sQuery(id+"F0.wireOp",EDGE,"E17.MirrorCS")])]}),makeQuery(id+"F1.opExtrude","SWEPT_FACE",FACE,{"disambiguationData":[OSD([sQuery(id+"F0.wireOp",EDGE,"E16.MirrorCS")])]})],"blendedInto":[makeQuery(id+"F1.opExtrude","SWEPT_FACE",FACE,{"disambiguationData":[OSD([sQuery(id+"F0.wireOp",EDGE,"E16.MirrorCS")])]})]});
            var Q3;
            Q3=makeQuery(id+"F1.opExtrude","SWEPT_EDGE",EDGE,{"disambiguationData":[OSD([sQuery(id+"F0.wireOp",EDGE,"E15.MirrorCS"),sQuery(id+"F0.wireOp",EDGE,"E16.MirrorCS")])]});
            var Q4;
            Q4=makeQuery(id+"F1.opExtrude","SWEPT_EDGE",EDGE,{"disambiguationData":[OSD([sQuery(id+"F0.wireOp",EDGE,"E9.0"),sQuery(id+"F0.wireOp",EDGE,"E10")])]});
            var Q5;
            Q5=makeQuery(id+"F1.opExtrude","SWEPT_EDGE",EDGE,{"disambiguationData":[OSD([sQuery(id+"F0.wireOp",EDGE,"E8.0"),sQuery(id+"F0.wireOp",EDGE,"E10")])]});
            var Q6;
            Q6=makeQuery(id+"F1.opExtrude","SWEPT_EDGE",EDGE,{"disambiguationData":[OSD([sQuery(id+"F0.wireOp",EDGE,"E11.1.0"),sQuery(id+"F0.wireOp",EDGE,"E11.1.1")])]});
            var Q7;
            Q7=makeQuery(id+"F1.opExtrude","SWEPT_EDGE",EDGE,{"disambiguationData":[OSD([sQuery(id+"F0.wireOp",EDGE,"E11.1.0"),sQuery(id+"F0.wireOp",EDGE,"E11.1.2")])]});
            var Q8;
            Q8=makeQuery(id+"F1.opExtrude","SWEPT_EDGE",EDGE,{"disambiguationData":[OSD([sQuery(id+"F0.wireOp",EDGE,"E11.2.0"),sQuery(id+"F0.wireOp",EDGE,"E11.2.1")])]});
            var Q9;
            Q9=makeQuery(id+"F5.opFillet","BLEND_EDGE",EDGE,{"blendedFrom":[makeQuery(id+"F1.opExtrude","SWEPT_EDGE",EDGE,{"disambiguationData":[OSD([sQuery(id+"F0.wireOp",EDGE,"E11.2.2"),sQuery(id+"F0.wireOp",EDGE,"E42.trimOffspring")])]}),makeQuery(id+"F1.opExtrude","SWEPT_FACE",FACE,{"disambiguationData":[OSD([sQuery(id+"F0.wireOp",EDGE,"E11.2.0")])]})],"blendedInto":[makeQuery(id+"F1.opExtrude","SWEPT_FACE",FACE,{"disambiguationData":[OSD([sQuery(id+"F0.wireOp",EDGE,"E11.2.0")])]})]});
            var Q10;
            Q10=makeQuery(id+"F5.opFillet","BLEND_EDGE",EDGE,{"blendedFrom":[makeQuery(id+"F1.opExtrude","SWEPT_EDGE",EDGE,{"disambiguationData":[OSD([sQuery(id+"F0.wireOp",EDGE,"E23.1.25"),sQuery(id+"F0.wireOp",EDGE,"E29.trimOffspring")])]}),makeQuery(id+"F1.opExtrude","SWEPT_FACE",FACE,{"disambiguationData":[OSD([sQuery(id+"F0.wireOp",EDGE,"E23.1.11")])]})],"blendedInto":[makeQuery(id+"F1.opExtrude","SWEPT_FACE",FACE,{"disambiguationData":[OSD([sQuery(id+"F0.wireOp",EDGE,"E23.1.11")])]})]});
            var Q11;
            Q11=makeQuery(id+"F1.opExtrude","SWEPT_EDGE",EDGE,{"disambiguationData":[OSD([sQuery(id+"F0.wireOp",EDGE,"E23.1.11"),sQuery(id+"F0.wireOp",EDGE,"E23.1.28")])]});
            var Q12;
            Q12=makeQuery(id+"F1.opExtrude","SWEPT_EDGE",EDGE,{"disambiguationData":[OSD([sQuery(id+"F0.wireOp",EDGE,"E23.1.12"),sQuery(id+"F0.wireOp",EDGE,"E23.1.19")])]});
            var Q13;
            Q13=makeQuery(id+"F1.opExtrude","SWEPT_EDGE",EDGE,{"disambiguationData":[OSD([sQuery(id+"F0.wireOp",EDGE,"E23.1.19"),sQuery(id+"F0.wireOp",EDGE,"E23.1.20")])]});
            var Q14;
            Q14=makeQuery(id+"F1.opExtrude","SWEPT_EDGE",EDGE,{"disambiguationData":[OSD([sQuery(id+"F0.wireOp",EDGE,"E23.1.16"),sQuery(id+"F0.wireOp",EDGE,"E23.1.17")])]});
            var Q15;
            Q15=makeQuery(id+"F1.opExtrude","SWEPT_EDGE",EDGE,{"disambiguationData":[OSD([sQuery(id+"F0.wireOp",EDGE,"E23.1.17"),sQuery(id+"F0.wireOp",EDGE,"E23.1.18")])]});
            var Q16;
            Q16=makeQuery(id+"F1.opExtrude","SWEPT_EDGE",EDGE,{"disambiguationData":[OSD([sQuery(id+"F0.wireOp",EDGE,"E23.1.14"),sQuery(id+"F0.wireOp",EDGE,"E23.1.24")])]});
            var Q17;
            Q17=makeQuery(id+"F1.opExtrude","SWEPT_EDGE",EDGE,{"disambiguationData":[OSD([sQuery(id+"F0.wireOp",EDGE,"E23.1.9"),sQuery(id+"F0.wireOp",EDGE,"E23.1.14")])]});
            var Q18;
            Q18=makeQuery(id+"F1.opExtrude","SWEPT_EDGE",EDGE,{"disambiguationData":[OSD([sQuery(id+"F0.wireOp",EDGE,"E23.1.23"),sQuery(id+"F0.wireOp",EDGE,"E23.1.27")])]});
            var Q19;
            Q19=makeQuery(id+"F5.opFillet","BLEND_EDGE",EDGE,{"blendedFrom":[makeQuery(id+"F1.opExtrude","SWEPT_EDGE",EDGE,{"disambiguationData":[OSD([sQuery(id+"F0.wireOp",EDGE,"E23.1.4"),sQuery(id+"F0.wireOp",EDGE,"E23.1.10")])]}),makeQuery(id+"F1.opExtrude","SWEPT_FACE",FACE,{"disambiguationData":[OSD([sQuery(id+"F0.wireOp",EDGE,"E23.1.23")])]})],"blendedInto":[makeQuery(id+"F1.opExtrude","SWEPT_FACE",FACE,{"disambiguationData":[OSD([sQuery(id+"F0.wireOp",EDGE,"E23.1.23")])]})]});
            var Q20;
            Q20=makeQuery(id+"F5.opFillet","BLEND_EDGE",EDGE,{"blendedFrom":[makeQuery(id+"F1.opExtrude","SWEPT_EDGE",EDGE,{"disambiguationData":[OSD([sQuery(id+"F0.wireOp",EDGE,"E23.2.25"),sQuery(id+"F0.wireOp",EDGE,"E46.trimOffspring")])]}),makeQuery(id+"F1.opExtrude","SWEPT_FACE",FACE,{"disambiguationData":[OSD([sQuery(id+"F0.wireOp",EDGE,"E23.2.11")])]})],"blendedInto":[makeQuery(id+"F1.opExtrude","SWEPT_FACE",FACE,{"disambiguationData":[OSD([sQuery(id+"F0.wireOp",EDGE,"E23.2.11")])]})]});
            var Q21;
            Q21=makeQuery(id+"F1.opExtrude","SWEPT_EDGE",EDGE,{"disambiguationData":[OSD([sQuery(id+"F0.wireOp",EDGE,"E23.2.11"),sQuery(id+"F0.wireOp",EDGE,"E23.2.28")])]});
            var Q22;
            Q22=makeQuery(id+"F1.opExtrude","SWEPT_EDGE",EDGE,{"disambiguationData":[OSD([sQuery(id+"F0.wireOp",EDGE,"E23.2.12"),sQuery(id+"F0.wireOp",EDGE,"E23.2.19")])]});
            var Q23;
            Q23=makeQuery(id+"F1.opExtrude","SWEPT_EDGE",EDGE,{"disambiguationData":[OSD([sQuery(id+"F0.wireOp",EDGE,"E23.2.19"),sQuery(id+"F0.wireOp",EDGE,"E23.2.20")])]});
            var Q24;
            Q24=makeQuery(id+"F1.opExtrude","SWEPT_EDGE",EDGE,{"disambiguationData":[OSD([sQuery(id+"F0.wireOp",EDGE,"E23.2.16"),sQuery(id+"F0.wireOp",EDGE,"E23.2.17")])]});
            var Q25;
            Q25=makeQuery(id+"F1.opExtrude","SWEPT_EDGE",EDGE,{"disambiguationData":[OSD([sQuery(id+"F0.wireOp",EDGE,"E23.2.17"),sQuery(id+"F0.wireOp",EDGE,"E23.2.18")])]});
            var Q26;
            Q26=makeQuery(id+"F1.opExtrude","SWEPT_EDGE",EDGE,{"disambiguationData":[OSD([sQuery(id+"F0.wireOp",EDGE,"E23.2.14"),sQuery(id+"F0.wireOp",EDGE,"E23.2.24")])]});
            var Q27;
            Q27=makeQuery(id+"F1.opExtrude","SWEPT_EDGE",EDGE,{"disambiguationData":[OSD([sQuery(id+"F0.wireOp",EDGE,"E23.2.9"),sQuery(id+"F0.wireOp",EDGE,"E23.2.14")])]});
            var Q28;
            Q28=makeQuery(id+"F1.opExtrude","SWEPT_EDGE",EDGE,{"disambiguationData":[OSD([sQuery(id+"F0.wireOp",EDGE,"E23.2.23"),sQuery(id+"F0.wireOp",EDGE,"E23.2.27")])]});
            var Q29;
            Q29=makeQuery(id+"F5.opFillet","BLEND_EDGE",EDGE,{"blendedFrom":[makeQuery(id+"F1.opExtrude","SWEPT_EDGE",EDGE,{"disambiguationData":[OSD([sQuery(id+"F0.wireOp",EDGE,"E23.2.4"),sQuery(id+"F0.wireOp",EDGE,"E23.2.10")])]}),makeQuery(id+"F1.opExtrude","SWEPT_FACE",FACE,{"disambiguationData":[OSD([sQuery(id+"F0.wireOp",EDGE,"E23.2.23")])]})],"blendedInto":[makeQuery(id+"F1.opExtrude","SWEPT_FACE",FACE,{"disambiguationData":[OSD([sQuery(id+"F0.wireOp",EDGE,"E23.2.23")])]})]});
            fillet(context, id + "F7", {"entities" : qUnion([Q0, Q1, Q2, Q3, Q4, Q5, Q6, Q7, Q8, Q9, Q10, Q11, Q12, Q13, Q14, Q15, Q16, Q17, Q18, Q19, Q20, Q21, Q22, Q23, Q24, Q25, Q26, Q27, Q28, Q29]), "radius" : 1 * mm, "tangentPropagation" : true, "allowEdgeOverflow" : false});
        }
        {
            var Q0;
            Q0=makeQuery(id+"F1.opExtrude","CAP_EDGE",EDGE,{"disambiguationData":[OSD([sQuery(id+"F0.wireOp",EDGE,"E41.1.0")])],"isStart":false});
            var Q1;
            Q1=makeQuery(id+"F1.opExtrude","CAP_EDGE",EDGE,{"disambiguationData":[OSD([sQuery(id+"F0.wireOp",EDGE,"E41.1.0")])],"isStart":true});
            chamfer(context, id + "F8", {"entities" : qUnion([Q0, Q1]), "width" : 1 * mm, "tangentPropagation" : true});
        }
        {
            var Q0;
            Q0=makeQuery(id+"F1.opExtrude","SWEPT_FACE",FACE,{"disambiguationData":[OSD([sQuery(id+"F0.wireOp",EDGE,"E41.1.0")])]});
            var sketch = newSketch(context, id + "F9", { "sketchPlane" : qUnion([Q0])});
            skText(sketch, "E48", { "text": "Maughanster V2.0", "fontName": "NotoSansCJKkr-Bold.otf"});
            skPoint(sketch, "E49", {"position": v(-18.42, 3.8) * mm});
            const initialGuessF9  = {"E48": [-0.01842, 0.0023, 1, 0, 0.003]};
            skSetInitialGuess(sketch, initialGuessF9);
            skSolve(sketch);
        }
        {
            var Q0;
            Q0=qSketchRegion(id+"F9",true);
            extrude(context, id + "F10", {"entities" : qUnion([Q0]), "operationType" : NewBodyOperationType.REMOVE, "oppositeDirection" : true, "depth" : .75 * mm});
        }
    });
